# Revit family: Valve Union Adaptor-JCI_Sapphire_Plus-(70bar)Novec1230
name_source: partatom
category: Specialty Equipment
revit_build: Autodesk Revit 2017 (Build: 20171027_0315(x64)
units: mm (PartAtom-declared; Revit-internal decimal feet)

## family parameters
Always vertical = No
Cut with Voids When Loaded = No
OmniClass Number = 23.29.33.13.11
Part Type = Normal
Room Calculation Point = No
Round Connector Dimension = Use Diameter
Shared = No
Work Plane-Based = No

## types (2) — shared parameters
Date Modified = YYYY/MM/DD
Discharge Flow = 0 GPM
Family Version = 1.0
Fire Suppression Agent = ''3M Novec'' 1230 Fire Protection Fluid
Manufacturer = Johnson Controls, Inc.
Material = JCI - Iron - Gray
Model Disclaimer = For More Information Contact JOHNSON CONTROLS
Operating Temperature = 122 °F
Product Documentation Link = http://www.sapphireplus.com
Product Material = JCI - Iron - Gray
Product Page URL = http://www.sapphireplus.com
URL = http://www.sapphireplus.com
Unit Assembly = Sapphire Plus_Valve Union Adapt

## per-type parameters (varying)
| type | Model | Union Adaptor Size | Weight |
| 25mm Valve Union Adaptor | 309002016 | 25 | 0.84 lbf |
| 50mm Valve Union Adaptor | 309002017 | 50 | 2.60 lbf |

note: column(s) folded — value = type name in every type: Description

## geometry (parser evidence)
native form markers: Sweep x2
no freeform markers — native parametric forms only
